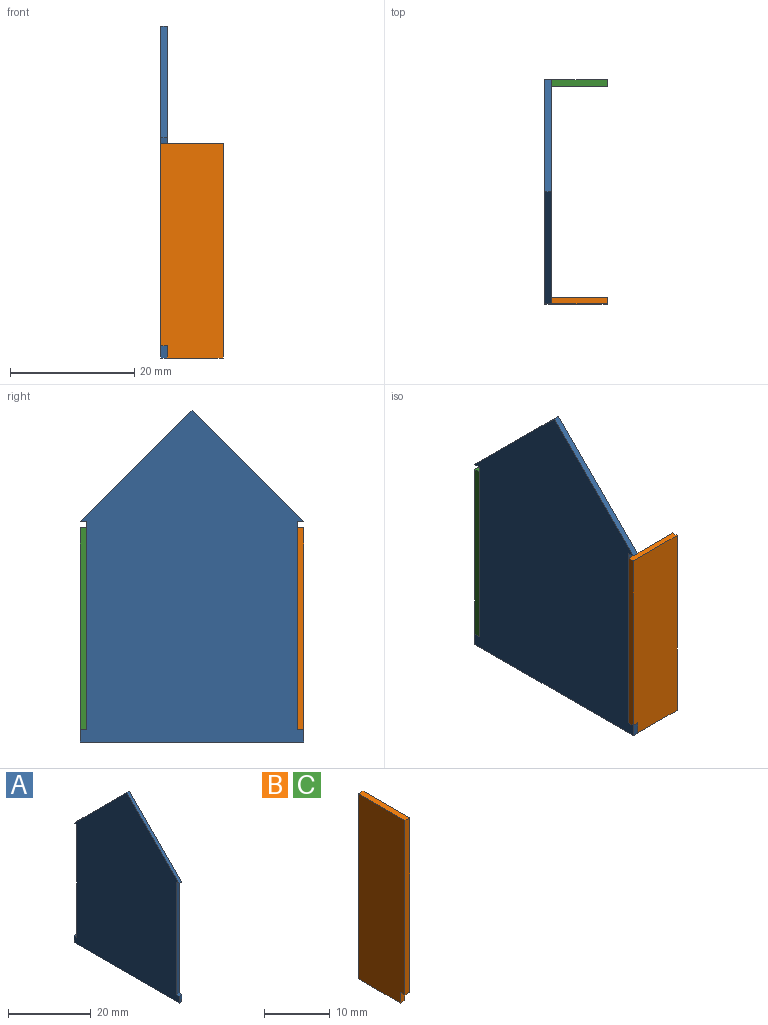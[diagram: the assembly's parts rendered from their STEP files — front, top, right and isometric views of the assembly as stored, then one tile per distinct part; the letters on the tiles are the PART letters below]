
ASSEMBLY  parts=3 mates=1
PART A: 13 faces, bbox 1x36x53.4 mm
  f0: plane 36x1mm, normal (0,0,-1), area 36mm2, adj f1,f10,f11,f12
  f1: plane 2x1mm, normal (0,1,0), area 2mm2, adj f0,f2,f11,f12
  f2: plane 1x1mm, normal (0,0,1), area 1mm2, adj f1,f3,f11,f12
  f3: plane 33.4x1mm, normal (0,1,0), area 33.4mm2, adj f2,f4,f11,f12
  f4: plane 1x1mm, normal (0,0,-1), area 1mm2, adj f3,f5,f11,f12
  f5: plane 18x18mm, normal (0,0.71,0.71), area 25.5mm2, adj f4,f6,f11,f12
  f6: plane 18x18mm, normal (0,-0.71,0.71), area 25.5mm2, adj f5,f7,f11,f12
  f7: plane 1x1mm, normal (0,0,-1), area 1mm2, adj f6,f8,f11,f12
  f8: plane 33.4x1mm, normal (0,-1,0), area 33.4mm2, adj f7,f9,f11,f12
  f9: plane 1x1mm, normal (0,0,1), area 1mm2, adj f8,f10,f11,f12
  f10: plane 2x1mm, normal (0,-1,0), area 2mm2, adj f0,f9,f11,f12
  f11: plane 53.4x36mm, normal (1,0,0), area 1531.6mm2, adj f0,f1,f2,f3,f4,f5,f6,f7
  f12: plane 53.4x36mm, normal (-1,0,0), area 1531.6mm2, adj f0,f1,f2,f3,f4,f5,f6,f7
PART B: 8 faces, bbox 1x10x34.4 mm
  f0: plane 34.43x1mm, normal (0,1,0), area 34.4mm2, adj f1,f5,f6,f7
  f1: plane 10x1mm, normal (0,0,1), area 10mm2, adj f0,f2,f6,f7
  f2: plane 32.43x1mm, normal (0,-1,0), area 32.4mm2, adj f1,f3,f6,f7
  f3: plane 1x1mm, normal (0,0,-1), area 1mm2, adj f2,f4,f6,f7
  f4: plane 2x1mm, normal (0,-1,0), area 2mm2, adj f3,f5,f6,f7
  f5: plane 9x1mm, normal (0,0,-1), area 9mm2, adj f0,f4,f6,f7
  f6: plane 34.43x10mm, normal (1,0,0), area 342.3mm2, adj f0,f1,f2,f3,f4,f5
  f7: plane 34.43x10mm, normal (-1,0,0), area 342.3mm2, adj f0,f1,f2,f3,f4,f5
PART C: same geometry as B
PLACE A rot(axis=(0,0,-1),180deg) t=(1.48,53.07,1.6)mm
PLACE B rot(axis=(0,0,-1),90deg) t=(-53.69,0.67,-6.8)mm
PLACE C rot(axis=(0,0,-1),90deg) t=(-53.69,35.67,-6.8)mm
MATE fastened B.f4 <-> A.f12  axis (-1,0,0) through (1.48,-0.33,17.46)mm
